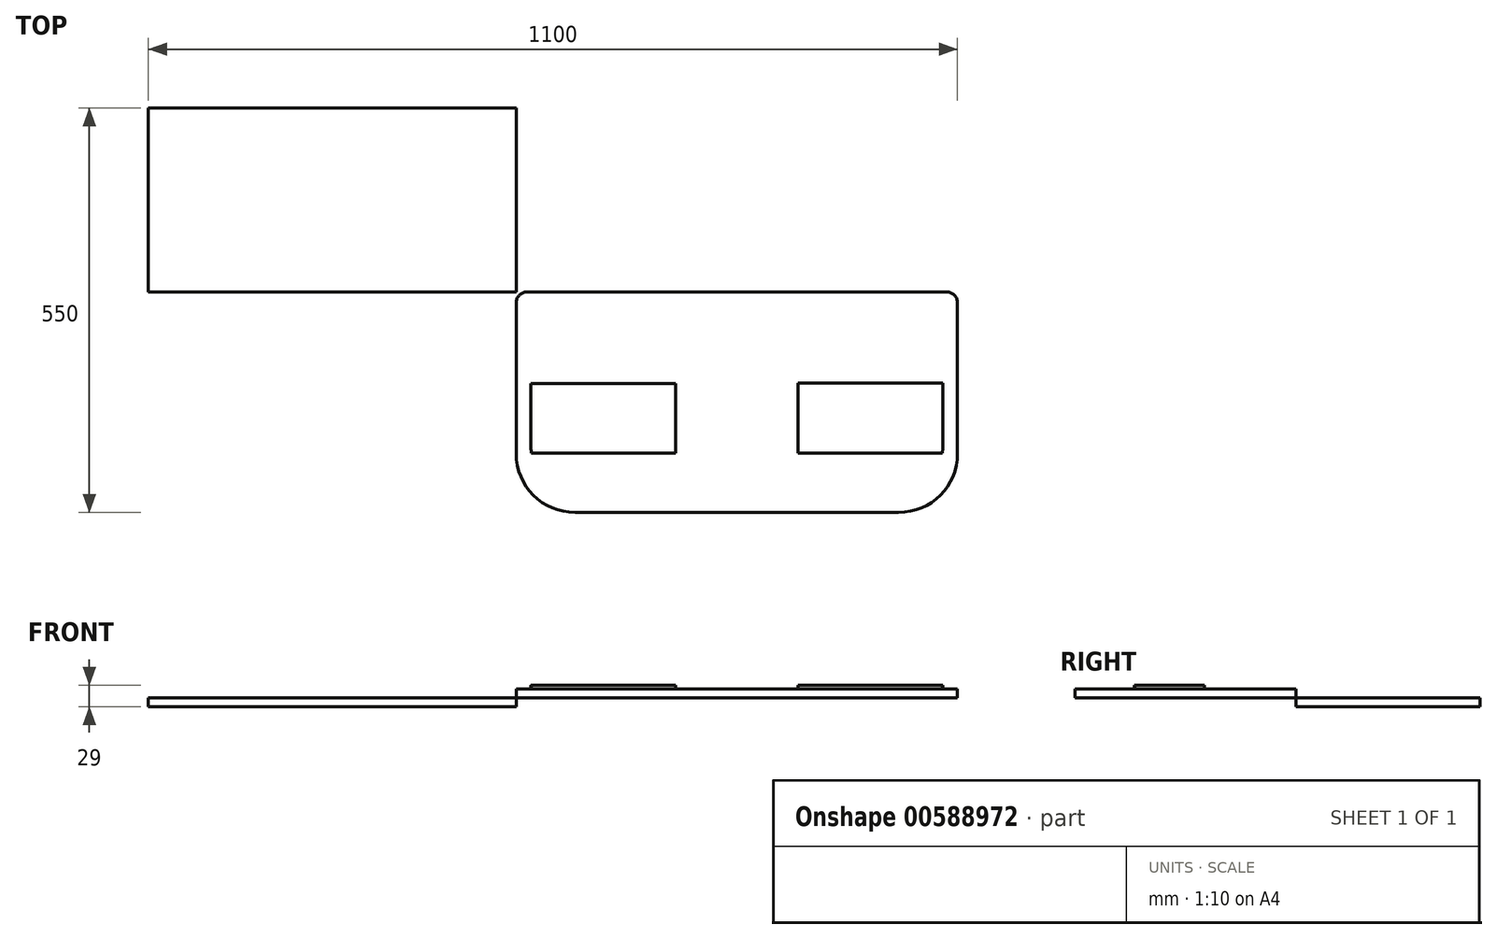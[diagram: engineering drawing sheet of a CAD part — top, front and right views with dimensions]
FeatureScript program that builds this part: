
annotation { "Feature Type Name" : "Feature", "Feature Type Description" : "" }
export const myFeature = defineFeature(function(context is Context, id is Id, definition is map)
    precondition{}
    {
        {
            var Q0;
            Q0=qCreatedBy(makeId("Top.planeOp"),FACE);
            var sketch = newSketch(context, id + "F0", { "sketchPlane" : qUnion([Q0])});
            skLineSegment(sketch, "E0.bottom", {"start": v(0, 0) * mm, "end": v(600, 0) * mm});
            skLineSegment(sketch, "E0.top", {"start": v(0, -300) * mm, "end": v(600, -300) * mm});
            skLineSegment(sketch, "E0.left", {"start": v(0, 0) * mm, "end": v(0, -300) * mm});
            skLineSegment(sketch, "E0.right", {"start": v(600, 0) * mm, "end": v(600, -300) * mm});
            skSolve(sketch);
        }
        {
            var Q0;
            Q0 = qSketchRegion(id + "F0", true);
            extrude(context, id + "F1", {"entities" : qUnion([Q0]), "depth" : 12 * mm, "offsetDistance" : 25 * mm});
        }
        {
            var Q0;
            Q0=makeQuery(id+"F1.opExtrude","SWEPT_EDGE",EDGE,{"disambiguationData":[OSD([sQuery(id+"F0.wireOp",EDGE,"E0.top"),sQuery(id+"F0.wireOp",EDGE,"E0.left")])]});
            var Q1;
            Q1=makeQuery(id+"F1.opExtrude","SWEPT_EDGE",EDGE,{"disambiguationData":[OSD([sQuery(id+"F0.wireOp",EDGE,"E0.top"),sQuery(id+"F0.wireOp",EDGE,"E0.right")])]});
            fillet(context, id + "F2", {"entities" : qUnion([Q0, Q1]), "radius" : 80 * mm, "tangentPropagation" : true, "allowEdgeOverflow" : false});
        }
        {
            var Q0;
            Q0=makeQuery(id+"F1.opExtrude","SWEPT_EDGE",EDGE,{"disambiguationData":[OSD([sQuery(id+"F0.wireOp",EDGE,"E0.bottom"),sQuery(id+"F0.wireOp",EDGE,"E0.left")])]});
            var Q1;
            Q1=makeQuery(id+"F1.opExtrude","SWEPT_EDGE",EDGE,{"disambiguationData":[OSD([sQuery(id+"F0.wireOp",EDGE,"E0.bottom"),sQuery(id+"F0.wireOp",EDGE,"E0.right")])]});
            fillet(context, id + "F3", {"entities" : qUnion([Q0, Q1]), "radius" : 15 * mm, "tangentPropagation" : true, "allowEdgeOverflow" : false});
        }
        {
            var Q0;
            Q0=makeQuery(id+"F1.opExtrude","SWEPT_BODY",BODY,{"disambiguationData":[OSD([sQuery(id+"F0.wireOp",EDGE,"E0.bottom"),sQuery(id+"F0.wireOp",EDGE,"E0.top"),sQuery(id+"F0.wireOp",EDGE,"E0.left"),sQuery(id+"F0.wireOp",EDGE,"E0.right")])]});
            transform(context, id + "F4", {"entities" : qUnion([Q0]), "transformType" : TransformType.TRANSLATION_3D, "dx" : 0 * mm, "dy" : 0 * mm, "dz" : 0 * mm, "makeCopy" : true});
        }
        {
            var Q0;
            Q0=qCreatedBy(makeId("Top.planeOp"),FACE);
            var sketch = newSketch(context, id + "F5", { "sketchPlane" : qUnion([Q0])});
            skLineSegment(sketch, "E1.bottom", {"start": v(0, 0) * mm, "end": v(-500, 0) * mm});
            skLineSegment(sketch, "E1.top", {"start": v(0, 250) * mm, "end": v(-500, 250) * mm});
            skLineSegment(sketch, "E1.left", {"start": v(0, 0) * mm, "end": v(0, 250) * mm});
            skLineSegment(sketch, "E1.right", {"start": v(-500, 0) * mm, "end": v(-500, 250) * mm});
            skSolve(sketch);
        }
        {
            var Q0;
            Q0=makeQuery(id+"F5.imprint","IMPRINT",FACE,{"disambiguationData":[TD([[makeQuery(id+"F5.imprint","IMPRINT",EDGE,{"derivedFrom":sQuery(id+"F5.wireOp",EDGE,"E1.bottom")}),-1.0]])]});
            extrude(context, id + "F6", {"entities" : qUnion([Q0]), "oppositeDirection" : true, "depth" : 12 * mm, "offsetDistance" : 25 * mm});
        }
        {
            var Q0;
            Q0=makeQuery(id+"F1.opExtrude","CAP_FACE",FACE,{"disambiguationData":[OSD([sQuery(id+"F0.wireOp",EDGE,"E0.bottom"),sQuery(id+"F0.wireOp",EDGE,"E0.top"),sQuery(id+"F0.wireOp",EDGE,"E0.left"),sQuery(id+"F0.wireOp",EDGE,"E0.right")])],"isStart":false});
            var sketch = newSketch(context, id + "F7", { "sketchPlane" : qUnion([Q0])});
            skLineSegment(sketch, "E2.bottom", {"start": v(0, -136.54) * mm, "end": v(197, -136.54) * mm});
            skLineSegment(sketch, "E2.top", {"start": v(0, -231.54) * mm, "end": v(197, -231.54) * mm});
            skLineSegment(sketch, "E2.left", {"start": v(0, -136.54) * mm, "end": v(0, -231.54) * mm});
            skLineSegment(sketch, "E2.right", {"start": v(197, -136.54) * mm, "end": v(197, -231.54) * mm});
            skLineSegment(sketch, "E3.bottom", {"start": v(600, -135.16) * mm, "end": v(403, -135.16) * mm});
            skLineSegment(sketch, "E3.top", {"start": v(600, -230.16) * mm, "end": v(403, -230.16) * mm});
            skLineSegment(sketch, "E3.left", {"start": v(600, -135.16) * mm, "end": v(600, -230.16) * mm});
            skLineSegment(sketch, "E3.right", {"start": v(403, -135.16) * mm, "end": v(403, -230.16) * mm});
            skSolve(sketch);
        }
        {
            var Q0;
            {var subQ5=sQuery(id+"F7.wireOp",EDGE,"E3.bottom");Q0=makeQuery(id+"F7.imprint","IMPRINT",FACE,{"disambiguationData":[TD([[makeQuery(id+"F7.imprint","IMPRINT",EDGE,{"derivedFrom":subQ5}),1.0]])]});}
            var Q1;
            {var subQ5=sQuery(id+"F7.wireOp",EDGE,"E2.bottom");Q1=makeQuery(id+"F7.imprint","IMPRINT",FACE,{"disambiguationData":[TD([[makeQuery(id+"F7.imprint","IMPRINT",EDGE,{"derivedFrom":subQ5}),-1.0]])]});}
            extrude(context, id + "F8", {"entities" : qUnion([Q0, Q1]), "depth" : 5 * mm, "offsetDistance" : 25 * mm});
        }
        {
            var Q0;
            Q0=makeQuery(id+"F8.opExtrude","SWEPT_BODY",BODY,{"disambiguationData":[OSD([sQuery(id+"F0.wireOp",EDGE,"E0.bottom"),sQuery(id+"F0.wireOp",EDGE,"E0.top"),sQuery(id+"F0.wireOp",EDGE,"E0.left"),sQuery(id+"F0.wireOp",EDGE,"E0.right"),sQuery(id+"F7.wireOp",EDGE,"E3.bottom"),sQuery(id+"F7.wireOp",EDGE,"E3.top"),sQuery(id+"F7.wireOp",EDGE,"E3.left"),sQuery(id+"F7.wireOp",EDGE,"E3.right")])]});
            transform(context, id + "F9", {"entities" : qUnion([Q0]), "transformType" : TransformType.TRANSLATION_3D, "dx" : 0 * mm, "dy" : 11 * mm, "dz" : 0 * mm, "makeCopy" : false});
        }
        {
            var Q0;
            Q0=makeQuery(id+"F8.opExtrude","SWEPT_BODY",BODY,{"disambiguationData":[OSD([sQuery(id+"F0.wireOp",EDGE,"E0.bottom"),sQuery(id+"F0.wireOp",EDGE,"E0.top"),sQuery(id+"F0.wireOp",EDGE,"E0.left"),sQuery(id+"F0.wireOp",EDGE,"E0.right"),sQuery(id+"F7.wireOp",EDGE,"E2.bottom"),sQuery(id+"F7.wireOp",EDGE,"E2.top"),sQuery(id+"F7.wireOp",EDGE,"E2.left"),sQuery(id+"F7.wireOp",EDGE,"E2.right")])]});
            transform(context, id + "F10", {"entities" : qUnion([Q0]), "transformType" : TransformType.TRANSLATION_3D, "dx" : 0 * mm, "dy" : 12 * mm, "dz" : 0 * mm, "makeCopy" : false});
        }
        {
            var Q0;
            Q0=makeQuery(id+"F8.opExtrude","SWEPT_BODY",BODY,{"disambiguationData":[OSD([sQuery(id+"F0.wireOp",EDGE,"E0.bottom"),sQuery(id+"F0.wireOp",EDGE,"E0.top"),sQuery(id+"F0.wireOp",EDGE,"E0.left"),sQuery(id+"F0.wireOp",EDGE,"E0.right"),sQuery(id+"F7.wireOp",EDGE,"E2.bottom"),sQuery(id+"F7.wireOp",EDGE,"E2.top"),sQuery(id+"F7.wireOp",EDGE,"E2.left"),sQuery(id+"F7.wireOp",EDGE,"E2.right")])]});
            transform(context, id + "F11", {"entities" : qUnion([Q0]), "transformType" : TransformType.TRANSLATION_3D, "dx" : 20 * mm, "dy" : 0 * mm, "dz" : 0 * mm, "makeCopy" : false});
        }
        {
            var Q0;
            Q0=makeQuery(id+"F8.opExtrude","SWEPT_BODY",BODY,{"disambiguationData":[OSD([sQuery(id+"F0.wireOp",EDGE,"E0.bottom"),sQuery(id+"F0.wireOp",EDGE,"E0.top"),sQuery(id+"F0.wireOp",EDGE,"E0.left"),sQuery(id+"F0.wireOp",EDGE,"E0.right"),sQuery(id+"F7.wireOp",EDGE,"E3.bottom"),sQuery(id+"F7.wireOp",EDGE,"E3.top"),sQuery(id+"F7.wireOp",EDGE,"E3.left"),sQuery(id+"F7.wireOp",EDGE,"E3.right")])]});
            transform(context, id + "F12", {"entities" : qUnion([Q0]), "transformType" : TransformType.TRANSLATION_3D, "dx" : -20 * mm, "dy" : 0 * mm, "dz" : 0 * mm, "makeCopy" : false});
        }
    });
